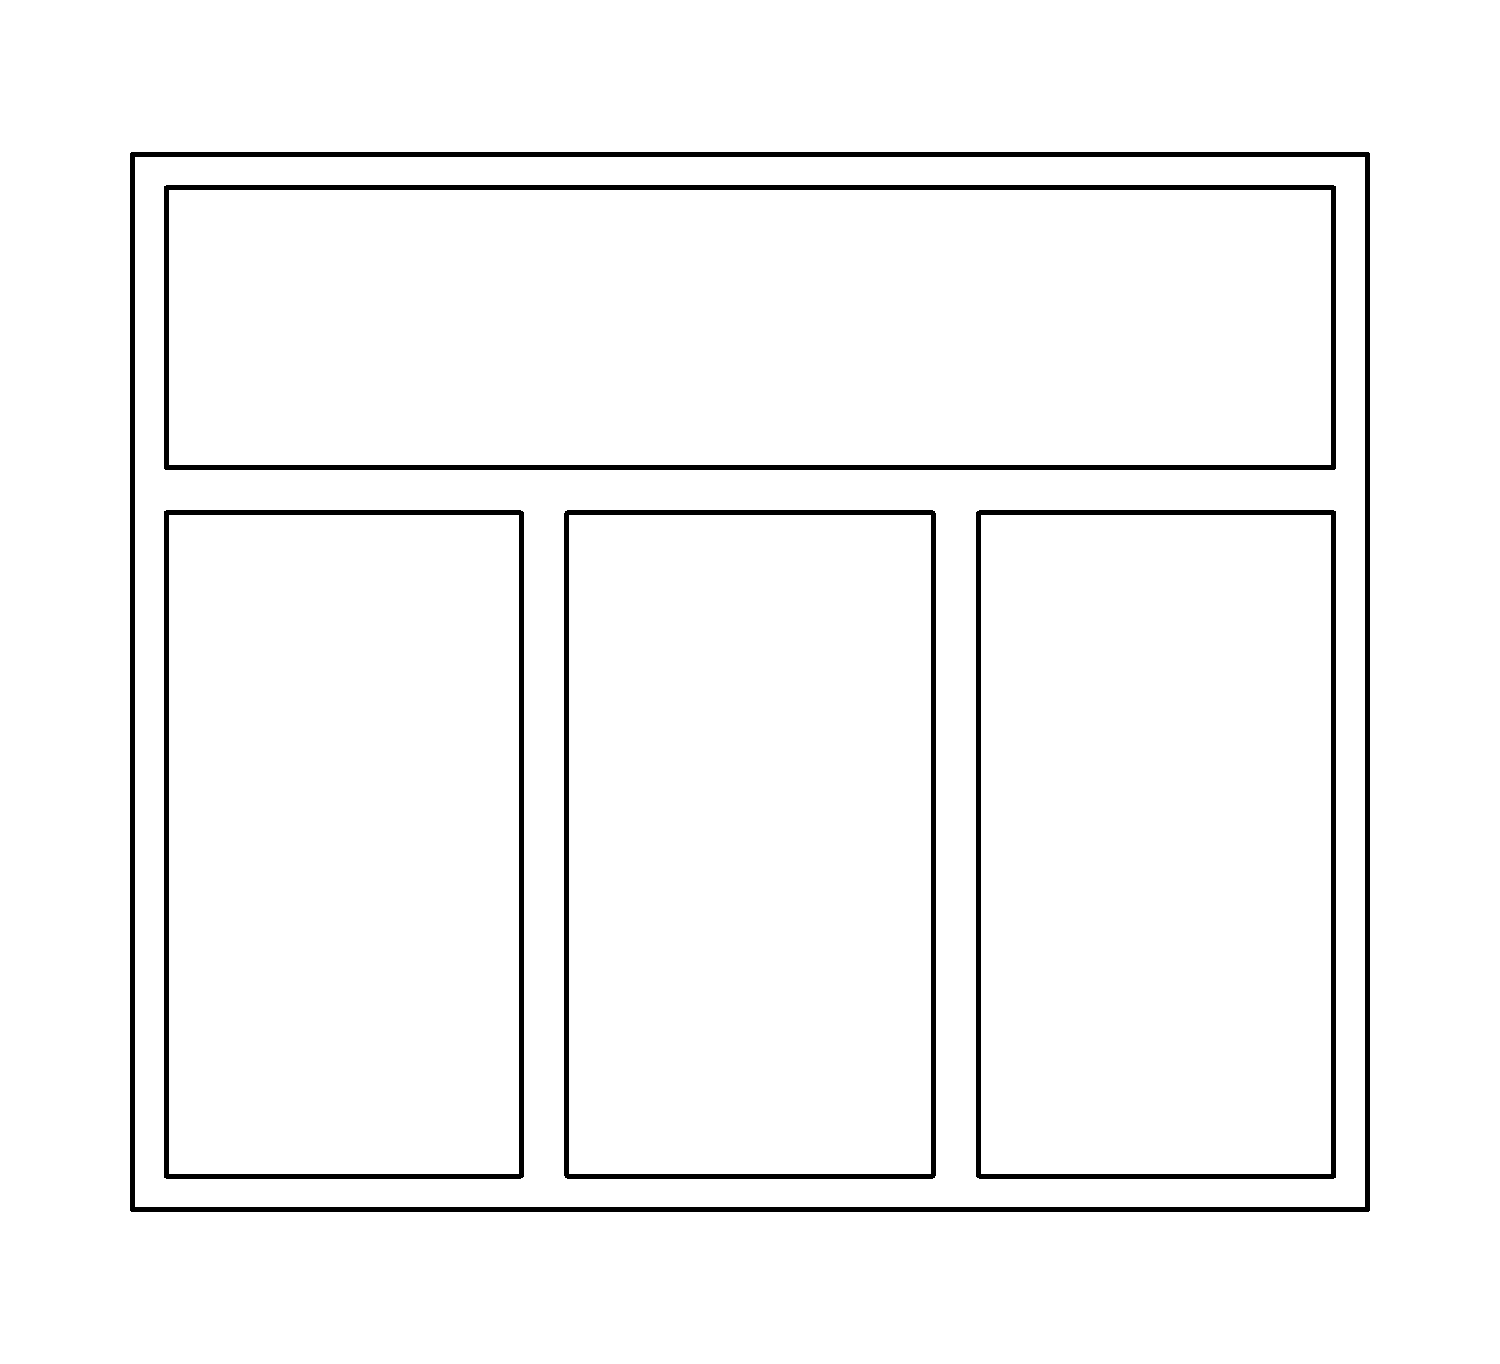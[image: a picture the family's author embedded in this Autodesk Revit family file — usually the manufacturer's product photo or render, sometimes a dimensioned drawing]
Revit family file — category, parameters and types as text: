
# Revit family: окна.rehau_трехпольное_фрамуга_сверху
name_source: partatom
category: Окна
revit_build: Autodesk Revit 2017 (Build: 20171027_0315(x64)
units: mm (PartAtom-declared; Revit-internal decimal feet)

## family parameters
Всегда вертикально = Да
Заголовок OmniClass = Windows
Номер OmniClass = 23.30.20.00
Общий = Нет
Основа = Стена
При загрузке вырезать с полостями = Нет
Точка расчета площади = Нет

## types (2) — shared parameters
24_мм = 24мм 1-камерный
32_мм = 32мм 2-камерный
40_мм = 40мм 2-камерный
42_мм = 42мм 2-камерный
50_мм = 50мм 2-камерный
60_blitz_new = 60 BLITZ NEW
60_euro_64 = 60 EURO (коробка 64, импост 78, створка 60)
60_euro_68 = 60 EURO (коробка 68, импост 78, створка 60)
60_euro_76 = 60 EURO (коробка 76, импост 86, створка 74)
70_delight_78 = 70 DELIGHT
70_grazio_55 = 70 GRAZIO (коробка 55)
70_grazio_63 = 70 GRAZIO (коробка 63)
80_intelio_58r = 80 INTELIO (коробка 58, створка R57)
80_intelio_58z = 80 INTELIO (коробка 58, створка Z57)
80_intelio_65r = 80 INTELIO (коробка 65, створка R57)
80_intelio_65z = 80 INTELIO (коробка 65, створка Z57)
ADSK_Обозначение = ГОСТ 30674-99
URL = https://www.rehau.com
sp_energy = Энергосберегающие стекла
sp_gaz = Заполненный газом
sp_standart = Обычный стеклопакет
sp_triplex = Триплекс
Аналитическая конструкция = Окна с одинарным остеклением - для жилых зданий
Высота подоконника по умолчанию = 900 мм
Высота створок = 1200 мм
Группа модели = ОП
Замыкание стены = По основе
Заполнение стеклопакета = Обычный стеклопакет
Изготовитель = Rehau
Изображение типоразмера = схема_трехпольное_фрамуга_сверху.png
Коэффициент теплопередачи (U) = 5.7361 Вт/(м²·K)
Коэффициент теплопритока от солнечного излучения = 0.86
Материал коробки = <По категории>
Материал отлива = <По категории>
Материал подоконника = <По категории>
Материал стекла = <По категории>
Описание = проем.окно
Примерная высота = 1760 мм
Примерная ширина = 2060 мм
Пропускание видимого света = 0.9
Равные створки = Да
Створка слева = 400 мм
Створка справа = 400 мм
Термостойкость = 0.1743 (м²·K)/Вт
Тип створки центр = створка : глухая
Тип фрамуги = створка : глухая
глухая_створка = створка : глухая
обозначение_проема_высота = 293 мм
обозначение_проема_ширина = 343 мм
таблица выбора = каталог профилей Rehau

## per-type parameters (varying)
| type | Тип створки слева | Тип створки справа |
| 2060х1760 (2 створки и глухое) | створка : левая-откидная | створка : правая-откидная |
| 2060х1760 (глухое) | створка : глухая | створка : глухая |
